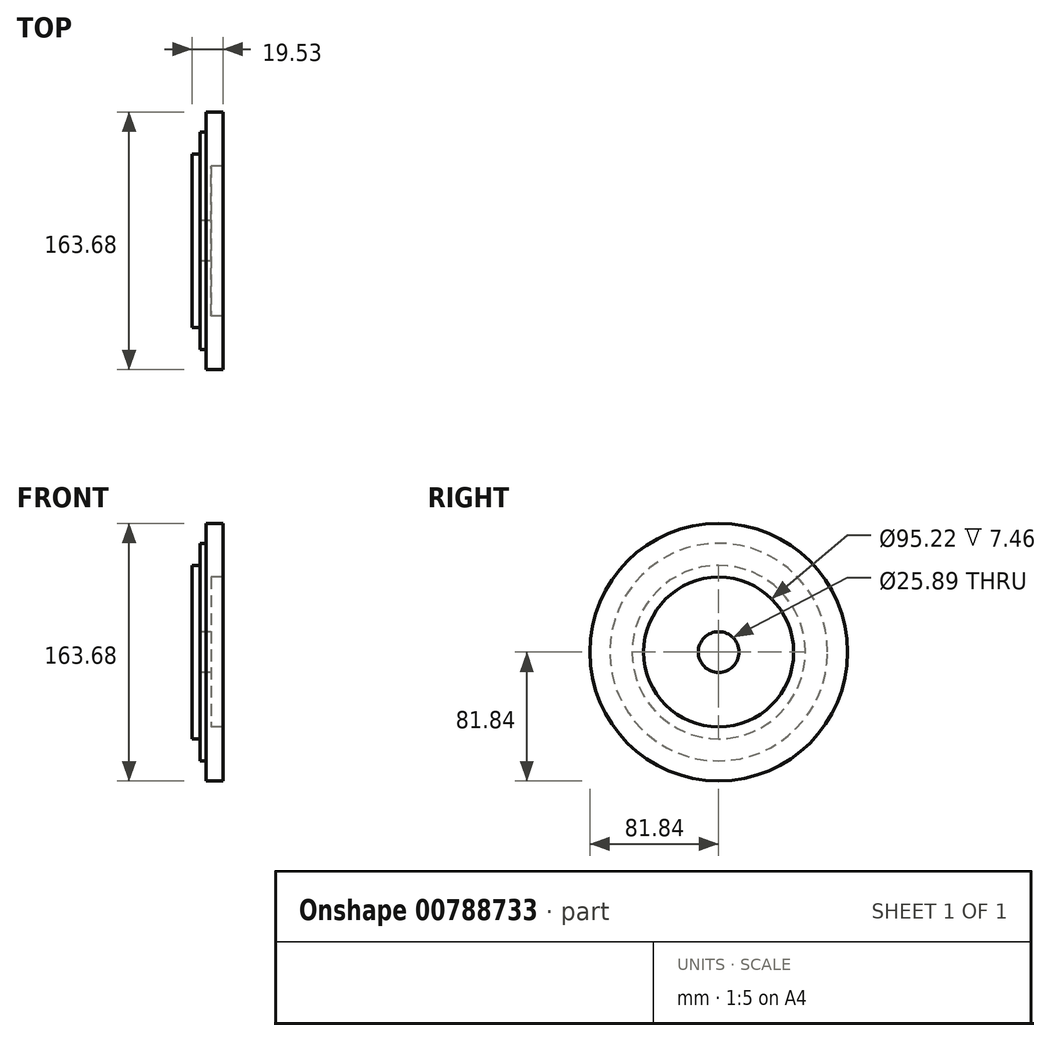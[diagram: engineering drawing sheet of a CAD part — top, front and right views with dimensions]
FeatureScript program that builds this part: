
annotation { "Feature Type Name" : "Feature", "Feature Type Description" : "" }
export const myFeature = defineFeature(function(context is Context, id is Id, definition is map)
    precondition{}
    {
        {
            var Q0;
            Q0=qCreatedBy(makeId("Front.planeOp"),FACE);
            var sketch = newSketch(context, id + "F0", { "sketchPlane" : qUnion([Q0])});
            skLineSegment(sketch, "E0", {"start": v(0, 12.94) * mm, "end": v(0, 55.07) * mm});
            skLineSegment(sketch, "E1", {"start": v(0, 55.07) * mm, "end": v(5.05, 55.07) * mm});
            skLineSegment(sketch, "E2", {"start": v(5.05, 55.07) * mm, "end": v(5.05, 69.11) * mm});
            skLineSegment(sketch, "E3", {"start": v(5.05, 69.11) * mm, "end": v(9, 69.11) * mm});
            skLineSegment(sketch, "E4", {"start": v(9, 69.11) * mm, "end": v(9, 81.84) * mm});
            skLineSegment(sketch, "E5", {"start": v(9, 81.84) * mm, "end": v(19.53, 81.84) * mm});
            skLineSegment(sketch, "E6", {"start": v(19.53, 81.84) * mm, "end": v(19.53, 47.6) * mm});
            skLineSegment(sketch, "E7", {"start": v(19.53, 47.6) * mm, "end": v(12.07, 47.6) * mm});
            skLineSegment(sketch, "E8", {"start": v(12.07, 47.6) * mm, "end": v(12.07, 12.94) * mm});
            skLineSegment(sketch, "E9", {"start": v(15.14, 12.94) * mm, "end": v(12.07, 12.94) * mm});
            skLineSegment(sketch, "E10", {"start": v(12.07, 12.94) * mm, "end": v(9, 12.94) * mm});
            skLineSegment(sketch, "E11", {"start": v(0, 12.94) * mm, "end": v(15.14, 12.94) * mm});
            skLineSegment(sketch, "E12", {"start": v(0, 0) * mm, "end": v(12.95, 0) * mm});
            skSolve(sketch);
        }
        {
            var Q0;
            Q0 = qSketchRegion(id + "F0", true);
            var Q1;
            Q1=sQuery(id+"F0.wireOp",EDGE,"E12");
            revolve(context, id + "F1", {"surfaceOperationType" : NewSurfaceOperationType.NEW, "entities" : qUnion([Q0]), "axis" : qUnion([Q1]), "revolveType" : RevolveType.FULL});
        }
    });
